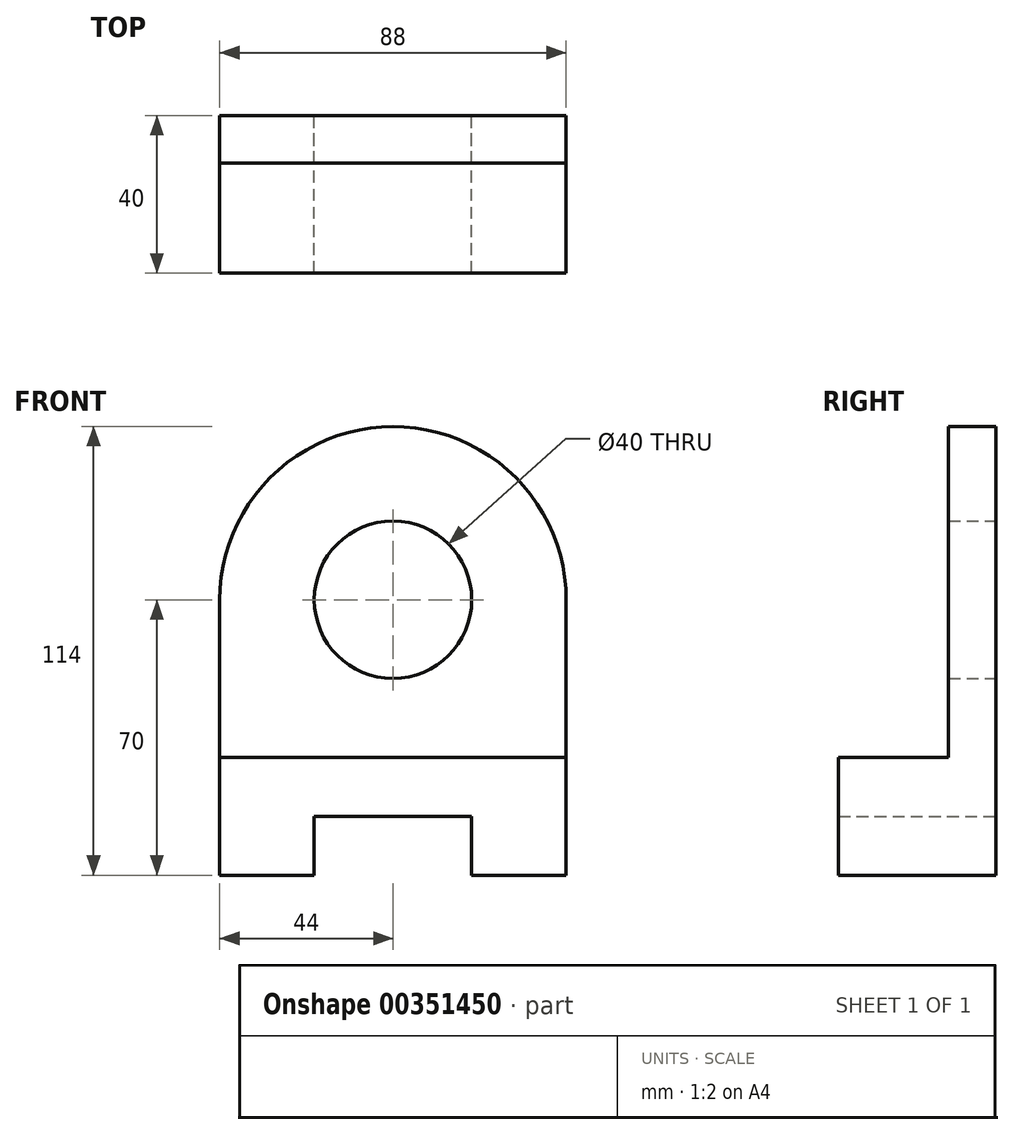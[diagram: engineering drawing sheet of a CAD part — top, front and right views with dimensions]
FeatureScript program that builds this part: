
annotation { "Feature Type Name" : "Feature", "Feature Type Description" : "" }
export const myFeature = defineFeature(function(context is Context, id is Id, definition is map)
    precondition{}
    {
        {
            var Q0;
            Q0=qCreatedBy(makeId("Front.planeOp"),FACE);
            var sketch = newSketch(context, id + "F0", { "sketchPlane" : qUnion([Q0])});
            skLineSegment(sketch, "E0", {"start": v(-44, 0) * mm, "end": v(-20, 0) * mm});
            skLineSegment(sketch, "E1", {"start": v(-20, 0) * mm, "end": v(-20, 15) * mm});
            skLineSegment(sketch, "E2", {"start": v(-20, 15) * mm, "end": v(20, 15) * mm});
            skLineSegment(sketch, "E3", {"start": v(20, 15) * mm, "end": v(20, 0) * mm});
            skLineSegment(sketch, "E4", {"start": v(20, 0) * mm, "end": v(44, 0) * mm});
            skLineSegment(sketch, "E5", {"start": v(-44, 0) * mm, "end": v(-44, 30) * mm});
            skLineSegment(sketch, "E6", {"start": v(-44, 30) * mm, "end": v(44, 30) * mm});
            skLineSegment(sketch, "E7", {"start": v(44, 30) * mm, "end": v(44, 0) * mm});
            skCircle(sketch, "E8", {"center": v(0, 70) * mm, "radius": 20 * mm});
            skLineSegment(sketch, "E9", {"start": v(-44, 30) * mm, "end": v(-44, 69.91) * mm});
            skLineSegment(sketch, "E10", {"start": v(44, 30) * mm, "end": v(44, 69.91) * mm});
            skArc(sketch, "E11", {"start": v(44, 69.91) * mm, "mid": v(0, 114) * mm, "end": v(-44, 69.91) * mm});
            skSolve(sketch);
        }
        {
            var Q0;
            Q0=makeQuery(id+"F0.imprint","IMPRINT",FACE,{"disambiguationData":[TD([[makeQuery(id+"F0.imprint","IMPRINT",EDGE,{"derivedFrom":sQuery(id+"F0.wireOp",EDGE,"E6")}),1.0]])]});
            extrude(context, id + "F1", {"entities" : qUnion([Q0]), "depth" : 12 * mm});
        }
        {
            var Q0;
            Q0=sQuery(id+"F0.wireOp",EDGE,"E8");
            extrude(context, id + "F2", {"bodyType" : ToolBodyType.SURFACE, "surfaceEntities" : qUnion([Q0]), "depth" : 28 * mm});
        }
        {
            var Q0;
            Q0=makeQuery(id+"F0.imprint","IMPRINT",FACE,{"disambiguationData":[TD([[makeQuery(id+"F0.imprint","IMPRINT",EDGE,{"derivedFrom":sQuery(id+"F0.wireOp",EDGE,"E0")}),1.0]])]});
            extrude(context, id + "F3", {"entities" : qUnion([Q0]), "operationType" : NewBodyOperationType.ADD, "depth" : 40 * mm});
        }
    });
